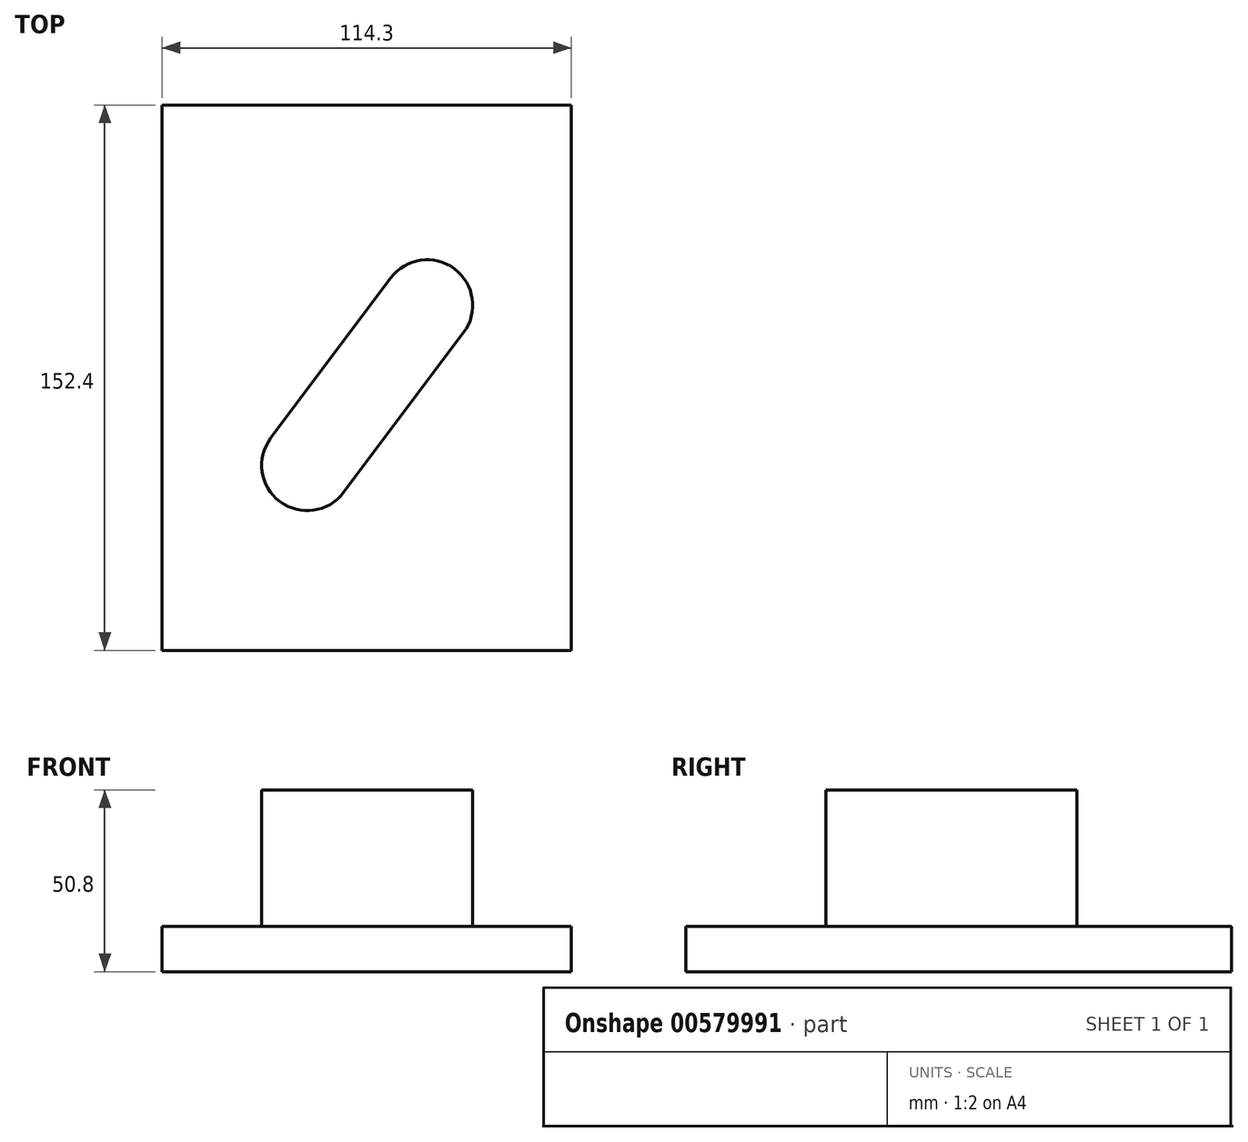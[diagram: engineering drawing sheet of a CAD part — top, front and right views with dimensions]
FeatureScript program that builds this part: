
annotation { "Feature Type Name" : "Feature", "Feature Type Description" : "" }
export const myFeature = defineFeature(function(context is Context, id is Id, definition is map)
    precondition{}
    {
        {
            var Q0;
            Q0=qCreatedBy(makeId("Top.planeOp"),FACE);
            var sketch = newSketch(context, id + "F0", { "sketchPlane" : qUnion([Q0])});
            skLineSegment(sketch, "E0.bottom", {"start": v(57.15, 76.2) * mm, "end": v(-57.15, 76.2) * mm});
            skLineSegment(sketch, "E0.top", {"start": v(57.15, -76.2) * mm, "end": v(-57.15, -76.2) * mm});
            skLineSegment(sketch, "E0.left", {"start": v(57.15, 76.2) * mm, "end": v(57.15, -76.2) * mm});
            skLineSegment(sketch, "E0.right", {"start": v(-57.15, 76.2) * mm, "end": v(-57.15, -76.2) * mm});
            skPoint(sketch, "E0.middle", {"position": v(0, 0) * mm});
            skLineSegment(sketch, "E1", {"start": v(57.15, 76.2) * mm, "end": v(-57.15, -76.2) * mm, "construction": true});
            skLineSegment(sketch, "E2", {"start": v(-6.47, -32.1) * mm, "end": v(27.06, 12.6) * mm});
            skLineSegment(sketch, "E3", {"start": v(27.06, 12.6) * mm, "end": v(6.74, 27.85) * mm});
            skLineSegment(sketch, "E4", {"start": v(-6.47, -32.1) * mm, "end": v(-26.8, -16.85) * mm});
            skLineSegment(sketch, "E5", {"start": v(-26.8, -16.85) * mm, "end": v(6.74, 27.85) * mm});
            skArc(sketch, "E6", {"start": v(27.06, 12.6) * mm, "mid": v(24.52, 30.39) * mm, "end": v(6.74, 27.85) * mm});
            skArc(sketch, "E7", {"start": v(-26.8, -16.85) * mm, "mid": v(-24.25, -34.63) * mm, "end": v(-6.47, -32.1) * mm});
            skLineSegment(sketch, "E8", {"start": v(-24.25, -34.63) * mm, "end": v(24.52, 30.39) * mm, "construction": true});
            skSolve(sketch);
        }
        {
            var Q0;
            Q0=makeQuery(id+"F0.imprint","IMPRINT",FACE,{"disambiguationData":[TD([[makeQuery(id+"F0.imprint","IMPRINT",EDGE,{"derivedFrom":sQuery(id+"F0.wireOp",EDGE,"E0.bottom")}),1.0]])]});
            extrude(context, id + "F1", {"entities" : qUnion([Q0]), "depth" : 12.7 * mm, "offsetDistance" : 25.4 * mm});
        }
        {
            var Q0;
            Q0=makeQuery(id+"F0.imprint","IMPRINT",FACE,{"disambiguationData":[TD([[makeQuery(id+"F0.imprint","IMPRINT",EDGE,{"derivedFrom":sQuery(id+"F0.wireOp",EDGE,"E3")}),-1.0]])]});
            var Q1;
            Q1=makeQuery(id+"F0.imprint","IMPRINT",FACE,{"disambiguationData":[TD([[makeQuery(id+"F0.imprint","IMPRINT",EDGE,{"derivedFrom":sQuery(id+"F0.wireOp",EDGE,"E2")}),1.0]])]});
            var Q2;
            Q2=makeQuery(id+"F0.imprint","IMPRINT",FACE,{"disambiguationData":[TD([[makeQuery(id+"F0.imprint","IMPRINT",EDGE,{"derivedFrom":sQuery(id+"F0.wireOp",EDGE,"E4")}),1.0]])]});
            extrude(context, id + "F2", {"entities" : qUnion([Q0, Q1, Q2]), "operationType" : NewBodyOperationType.ADD, "depth" : 50.8 * mm, "offsetDistance" : 25.4 * mm});
        }
    });
